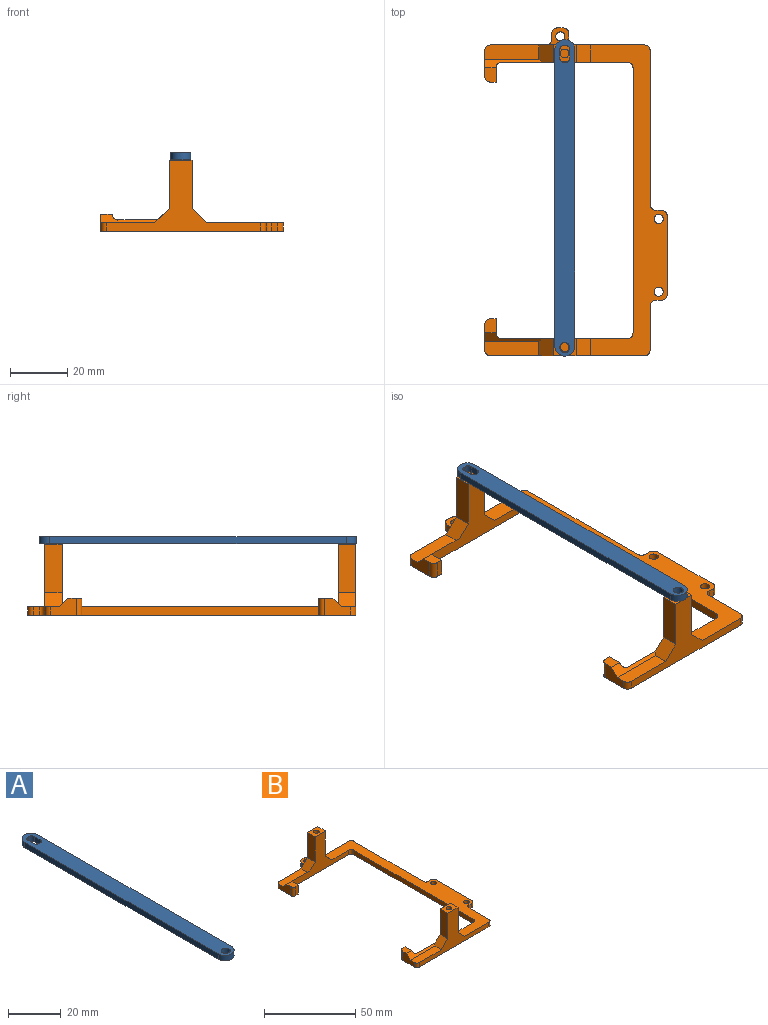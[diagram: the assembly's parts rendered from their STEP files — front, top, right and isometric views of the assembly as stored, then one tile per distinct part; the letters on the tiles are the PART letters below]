
ASSEMBLY  parts=2 mates=1
PART A: 15 faces, bbox 7x111x2.5 mm
  f0: plane 104x2.5mm, normal (1,0,0), area 260mm2, adj f7,f8,f13,f14
  f1: plane 2.5x0.5mm, normal (0,-1,0), area 1.2mm2, adj f7,f8,f9,f12
  f2: plane 3x2.5mm, normal (-1,0,0), area 7.5mm2, adj f7,f8,f9,f10
  f3: plane 2.5x0.5mm, normal (0,1,0), area 1.2mm2, adj f7,f8,f10,f11
  f4: cylinder r=1.75mm len=3.5mm, axis (0,0,-1), area 27.5mm2, adj f7,f8
  f5: plane 3x2.5mm, normal (1,0,0), area 7.5mm2, adj f7,f8,f11,f12
  f6: plane 104x2.5mm, normal (-1,0,0), area 260mm2, adj f7,f8,f13,f14
  f7: plane 111x7mm, normal (0,0,1), area 737.8mm2, adj f0,f1,f2,f3,f4,f5,f6,f9
  f8: plane 111x7mm, normal (0,0,-1), area 737.8mm2, adj f0,f1,f2,f3,f4,f5,f6,f9
  f9: cylinder r=1.5mm len=2.5mm, axis (0,0,-1), area 5.9mm2, adj f1,f2,f7,f8
  f10: cylinder r=1.5mm len=2.5mm, axis (0,0,1), area 5.9mm2, adj f2,f3,f7,f8
  f11: cylinder r=1.5mm len=2.5mm, axis (0,0,-1), area 5.9mm2, adj f3,f5,f7,f8
  f12: cylinder r=1.5mm len=2.5mm, axis (0,0,1), area 5.9mm2, adj f1,f5,f7,f8
  f13: cylinder r=3.5mm len=7mm, axis (0,0,-1), area 27.5mm2, adj f0,f6,f7,f8
  f14: cylinder r=3.5mm len=7mm, axis (0,0,1), area 27.5mm2, adj f0,f6,f7,f8
PART B: 64 faces, bbox 64x115x25 mm
  f0: plane 19x5mm, normal (0,0,1), area 94.1mm2, adj f12,f13,f40,f48,f62
  f1: plane 109x27mm, normal (0,0,1), area 1006.9mm2, adj f3,f4,f5,f6,f7,f8,f16,f17
  f2: plane 10x6mm, normal (0,0,1), area 28mm2, adj f8,f9,f10,f11,f23,f46,f47,f58
  f3: plane 15.5x3mm, normal (1,0,0), area 46.5mm2, adj f1,f27,f56,f57
  f4: plane 3x2mm, normal (0,-1,0), area 6mm2, adj f1,f27,f57,f60
  f5: plane 27.5x3mm, normal (1,0,0), area 82.5mm2, adj f1,f27,f60,f61
  f6: plane 3x2mm, normal (0,1,0), area 6mm2, adj f1,f27,f44,f61
  f7: plane 54x3mm, normal (1,0,0), area 162mm2, adj f1,f27,f44,f45
  f8: plane 37x25mm, normal (0,1,0), area 274.5mm2, adj f1,f2,f12,f27,f28,f29,f30,f40
  f9: plane 3x2mm, normal (1,0,0), area 6mm2, adj f2,f27,f46,f58
  f10: plane 3x2mm, normal (0,1,0), area 6mm2, adj f2,f27,f58,f59
  f11: plane 3x2mm, normal (-1,0,0), area 6mm2, adj f2,f27,f47,f59
  f12: plane 19.5x3mm, normal (0,1,0), area 58.5mm2, adj f0,f8,f27,f47,f48
  f13: plane 9x6mm, normal (-1,0,0), area 40.5mm2, adj f0,f27,f43,f48,f49,f62
  f14: plane 6x2mm, normal (0,-1,0), area 12mm2, adj f15,f27,f43,f49
  f15: plane 6x5mm, normal (1,0,0), area 30mm2, adj f14,f27,f43,f50
  f16: plane 44x25mm, normal (0,-1,0), area 346.5mm2, adj f1,f27,f28,f29,f30,f40,f41,f50
  f17: plane 93x3mm, normal (-1,0,0), area 279mm2, adj f1,f27,f51,f52
  f18: plane 44x25mm, normal (0,1,0), area 346.5mm2, adj f1,f27,f31,f32,f33,f38,f39,f52
  f19: plane 6x5mm, normal (1,0,0), area 30mm2, adj f20,f27,f42,f53
  f20: plane 6x2mm, normal (0,1,0), area 12mm2, adj f19,f27,f42,f54
  f21: plane 9x6mm, normal (-1,0,0), area 40.5mm2, adj f26,f27,f42,f54,f55,f63
  f22: cylinder r=1.6mm len=3.2mm, axis (0,0,-1), area 30.2mm2, adj f1,f27
  f23: cylinder r=1.6mm len=3.2mm, axis (0,0,-1), area 30.2mm2, adj f2,f27
  f24: plane 54x25mm, normal (0,-1,0), area 363mm2, adj f1,f26,f27,f31,f32,f33,f38,f39
  f25: cylinder r=1.6mm len=3.2mm, axis (0,0,-1), area 30.2mm2, adj f1,f27
  f26: plane 19x5mm, normal (0,0,1), area 94.1mm2, adj f21,f24,f38,f55,f63
  f27: plane 115x64mm, normal (0,0,-1), area 1533.2mm2, adj f3,f4,f5,f6,f7,f8,f9,f10
  f28: plane 17x6mm, normal (-1,0,0), area 102mm2, adj f8,f16,f30,f40
  f29: plane 17x6mm, normal (1,0,0), area 102mm2, adj f8,f16,f30,f41
  f30: plane 8x6mm, normal (0,0,1), area 40.5mm2, adj f8,f16,f28,f29,f34
  f31: plane 17x6mm, normal (-1,0,0), area 102mm2, adj f18,f24,f33,f38
  f32: plane 17x6mm, normal (1,0,0), area 102mm2, adj f18,f24,f33,f39
  f33: plane 8x6mm, normal (0,0,1), area 40.5mm2, adj f18,f24,f31,f32,f36
  f34: cylinder r=1.55mm len=10mm, axis (0,0,1), area 97.4mm2, adj f30,f35
  f35: plane 3.1x3.1mm, normal (0,0,1), area 7.5mm2, adj f34
  f36: cylinder r=1.55mm len=10mm, axis (0,0,1), area 97.4mm2, adj f33,f37
  f37: plane 3.1x3.1mm, normal (0,0,1), area 7.5mm2, adj f36
  f38: plane 6x5mm, normal (-0.71,0,0.71), area 41.7mm2, adj f18,f24,f26,f31,f63
  f39: plane 6x5mm, normal (0.71,0,0.71), area 42.4mm2, adj f1,f18,f24,f32
  f40: plane 6x5mm, normal (-0.71,0,0.71), area 41.7mm2, adj f0,f8,f16,f28,f62
  f41: plane 6x5mm, normal (0.71,0,0.71), area 42.4mm2, adj f1,f8,f16,f29
  f42: plane 5x4mm, normal (0,0,1), area 19.1mm2, adj f19,f20,f21,f54,f63
  f43: plane 5x4mm, normal (0,0,1), area 19.1mm2, adj f13,f14,f15,f49,f62
  f44: cylinder r=2mm len=3mm, axis (0,0,1), area 9.4mm2, adj f1,f6,f7,f27
  f45: cylinder r=2mm len=3mm, axis (0,0,-1), area 9.4mm2, adj f1,f7,f8,f27
  f46: cylinder r=2mm len=3mm, axis (0,0,-1), area 9.4mm2, adj f2,f8,f9,f27
  f47: cylinder r=2mm len=3mm, axis (0,0,1), area 9.4mm2, adj f2,f11,f12,f27
  f48: cylinder r=2mm len=3mm, axis (0,0,-1), area 9.4mm2, adj f0,f12,f13,f27
  f49: cylinder r=2mm len=6mm, axis (0,0,-1), area 18.8mm2, adj f13,f14,f27,f43
  f50: cylinder r=2mm len=6mm, axis (0,0,1), area 14.8mm2, adj f15,f16,f27,f62
  f51: cylinder r=2mm len=3mm, axis (0,0,1), area 9.4mm2, adj f1,f16,f17,f27
  f52: cylinder r=2mm len=3mm, axis (0,0,1), area 9.4mm2, adj f1,f17,f18,f27
  f53: cylinder r=2mm len=6mm, axis (0,0,1), area 14.8mm2, adj f18,f19,f27,f63
  f54: cylinder r=2mm len=6mm, axis (0,0,-1), area 18.8mm2, adj f20,f21,f27,f42
  f55: cylinder r=2mm len=3mm, axis (0,0,-1), area 9.4mm2, adj f21,f24,f26,f27
  f56: cylinder r=2mm len=3mm, axis (0,0,-1), area 9.4mm2, adj f1,f3,f24,f27
  f57: cylinder r=2mm len=3mm, axis (0,0,-1), area 9.4mm2, adj f1,f3,f4,f27
  f58: cylinder r=2mm len=3mm, axis (0,0,1), area 9.4mm2, adj f2,f9,f10,f27
  f59: cylinder r=2mm len=3mm, axis (0,0,-1), area 9.4mm2, adj f2,f10,f11,f27
  f60: cylinder r=2mm len=3mm, axis (0,0,1), area 9.4mm2, adj f1,f4,f5,f27
  f61: cylinder r=2mm len=3mm, axis (0,0,-1), area 9.4mm2, adj f1,f5,f6,f27
  f62: plane 20x3mm, normal (0,0.71,0.71), area 40.1mm2, adj f0,f13,f16,f40,f43,f50
  f63: plane 20x3mm, normal (0,-0.71,0.71), area 40.1mm2, adj f18,f21,f26,f38,f42,f53
PLACE A t=(16.53,-86.9,36.08)mm
PLACE B t=(-7.54,-59.39,10.98)mm
MATE parallel B.f30 <-> A.f8  axis (0,0,1) through (16.46,13.26,35.98)mm
